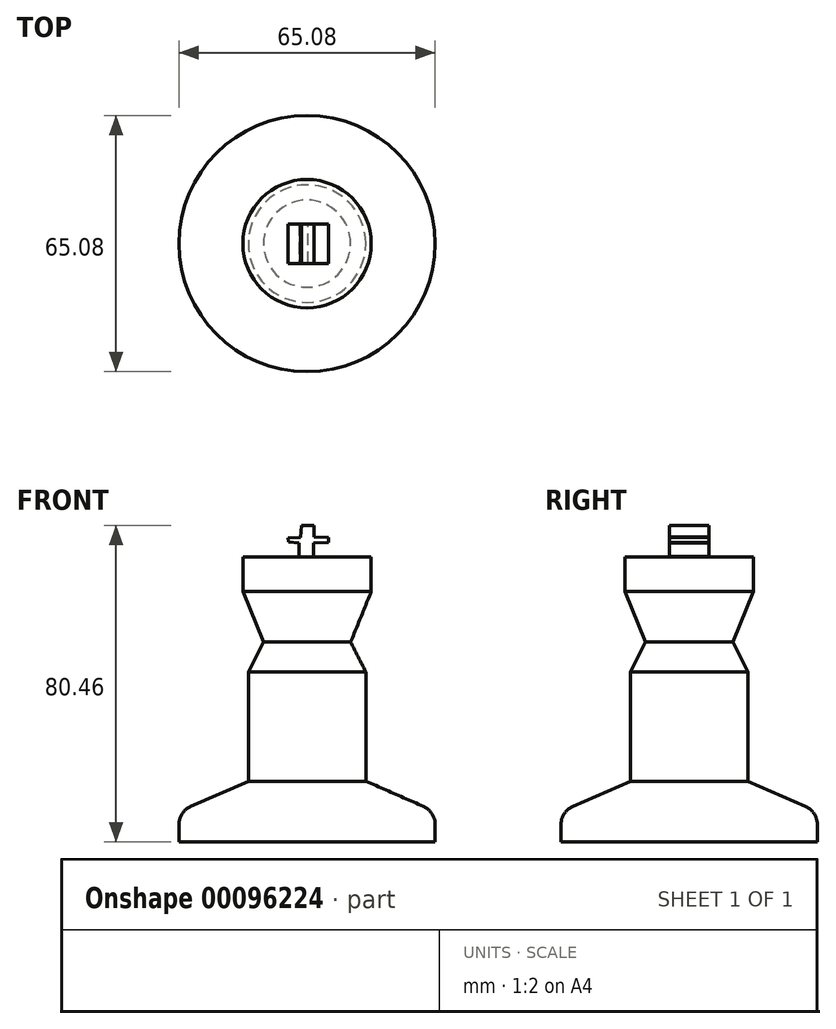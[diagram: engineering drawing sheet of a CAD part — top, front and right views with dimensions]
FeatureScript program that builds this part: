
annotation { "Feature Type Name" : "Feature", "Feature Type Description" : "" }
export const myFeature = defineFeature(function(context is Context, id is Id, definition is map)
    precondition{}
    {
        {
            var Q0;
            Q0=qCreatedBy(makeId("Front.planeOp"),FACE);
            var sketch = newSketch(context, id + "F0", { "sketchPlane" : qUnion([Q0])});
            skLineSegment(sketch, "E0", {"start": v(0, -50.76) * mm, "end": v(-32.54, -50.76) * mm});
            skLineSegment(sketch, "E1", {"start": v(-32.54, -50.76) * mm, "end": v(-32.54, -46.32) * mm});
            skLineSegment(sketch, "E2", {"start": v(-29.55, -41.74) * mm, "end": v(-14.93, -35.35) * mm});
            skLineSegment(sketch, "E3", {"start": v(-14.93, -35.35) * mm, "end": v(-14.93, -7.54) * mm});
            skLineSegment(sketch, "E4", {"start": v(-14.93, -7.54) * mm, "end": v(-11.07, 0) * mm});
            skLineSegment(sketch, "E5", {"start": v(-11.07, 0) * mm, "end": v(-16.3, 12.83) * mm});
            skLineSegment(sketch, "E6", {"start": v(-16.3, 12.83) * mm, "end": v(-16.3, 21.64) * mm});
            skLineSegment(sketch, "E7", {"start": v(-16.3, 21.64) * mm, "end": v(0, 21.64) * mm});
            skLineSegment(sketch, "E8", {"start": v(0, 21.64) * mm, "end": v(0, -50.76) * mm});
            skPoint(sketch, "E9.visualSharp", {"position": v(-32.54, -43.05) * mm});
            skArc(sketch, "E9.filletArc", {"start": v(-29.55, -41.74) * mm, "mid": v(-31.73, -43.59) * mm, "end": v(-32.54, -46.32) * mm});
            skSolve(sketch);
        }
        {
            var Q0;
            Q0 = qSketchRegion(id + "F0", true);
            var Q1;
            Q1=sQuery(id+"F0.wireOp",EDGE,"E8");
            revolve(context, id + "F1", {"entities" : qUnion([Q0]), "axis" : qUnion([Q1]), "revolveType" : RevolveType.FULL});
        }
        {
            var Q0;
            Q0=qCreatedBy(makeId("Front.planeOp"),FACE);
            var sketch = newSketch(context, id + "F2", { "sketchPlane" : qUnion([Q0])});
            skLineSegment(sketch, "E10", {"start": v(1.65, 21.73) * mm, "end": v(1.65, 25.25) * mm});
            skLineSegment(sketch, "E11", {"start": v(1.65, 25.25) * mm, "end": v(5.5, 25.33) * mm});
            skLineSegment(sketch, "E12", {"start": v(5.5, 25.33) * mm, "end": v(5.5, 26.6) * mm});
            skLineSegment(sketch, "E13", {"start": v(5.5, 26.6) * mm, "end": v(1.73, 26.68) * mm});
            skLineSegment(sketch, "E14", {"start": v(1.73, 26.68) * mm, "end": v(1.82, 29.61) * mm});
            skLineSegment(sketch, "E15", {"start": v(1.82, 29.61) * mm, "end": v(-1.45, 29.7) * mm});
            skLineSegment(sketch, "E16", {"start": v(-1.45, 29.7) * mm, "end": v(-1.62, 26.6) * mm});
            skLineSegment(sketch, "E17", {"start": v(-1.62, 26.6) * mm, "end": v(-4.8, 26.5) * mm});
            skLineSegment(sketch, "E18", {"start": v(-4.8, 26.5) * mm, "end": v(-4.72, 25.5) * mm});
            skLineSegment(sketch, "E19", {"start": v(-4.72, 25.5) * mm, "end": v(-2.04, 25.17) * mm});
            skLineSegment(sketch, "E20", {"start": v(-2.04, 25.17) * mm, "end": v(-2.04, 21.48) * mm});
            skLineSegment(sketch, "E21", {"start": v(-2.04, 21.48) * mm, "end": v(1.65, 21.73) * mm});
            skSolve(sketch);
        }
        {
            var Q0;
            Q0 = qSketchRegion(id + "F2", true);
            extrude(context, id + "F3", {"entities" : qUnion([Q0]), "operationType" : NewBodyOperationType.ADD, "depth" : 5 * mm});
        }
        {
            var Q0;
            Q0=makeQuery(id+"F1.opRevolve","SWEPT_BODY",BODY,{"disambiguationData":[OSD([sQuery(id+"F0.wireOp",EDGE,"E0"),sQuery(id+"F0.wireOp",EDGE,"E1"),sQuery(id+"F0.wireOp",EDGE,"E2"),sQuery(id+"F0.wireOp",EDGE,"E3"),sQuery(id+"F0.wireOp",EDGE,"E4"),sQuery(id+"F0.wireOp",EDGE,"E5"),sQuery(id+"F0.wireOp",EDGE,"E6"),sQuery(id+"F0.wireOp",EDGE,"E7"),sQuery(id+"F0.wireOp",EDGE,"E8"),sQuery(id+"F0.wireOp",EDGE,"E9.filletArc")])]});
            var Q1;
            Q1=makeQuery(id+"F3.opExtrude","CAP_FACE",FACE,{"disambiguationData":[OSD([sQuery(id+"F2.wireOp",EDGE,"E10"),sQuery(id+"F2.wireOp",EDGE,"E11"),sQuery(id+"F2.wireOp",EDGE,"E12"),sQuery(id+"F2.wireOp",EDGE,"E13"),sQuery(id+"F2.wireOp",EDGE,"E14"),sQuery(id+"F2.wireOp",EDGE,"E15"),sQuery(id+"F2.wireOp",EDGE,"E16"),sQuery(id+"F2.wireOp",EDGE,"E17"),sQuery(id+"F2.wireOp",EDGE,"E18"),sQuery(id+"F2.wireOp",EDGE,"E19"),sQuery(id+"F2.wireOp",EDGE,"E20"),sQuery(id+"F2.wireOp",EDGE,"E21")])],"isStart":true});
            mirror(context, id + "F4", {"operationType" : NewBodyOperationType.ADD, "entities" : qUnion([Q0]), "mirrorPlane" : qUnion([Q1])});
        }
    });
